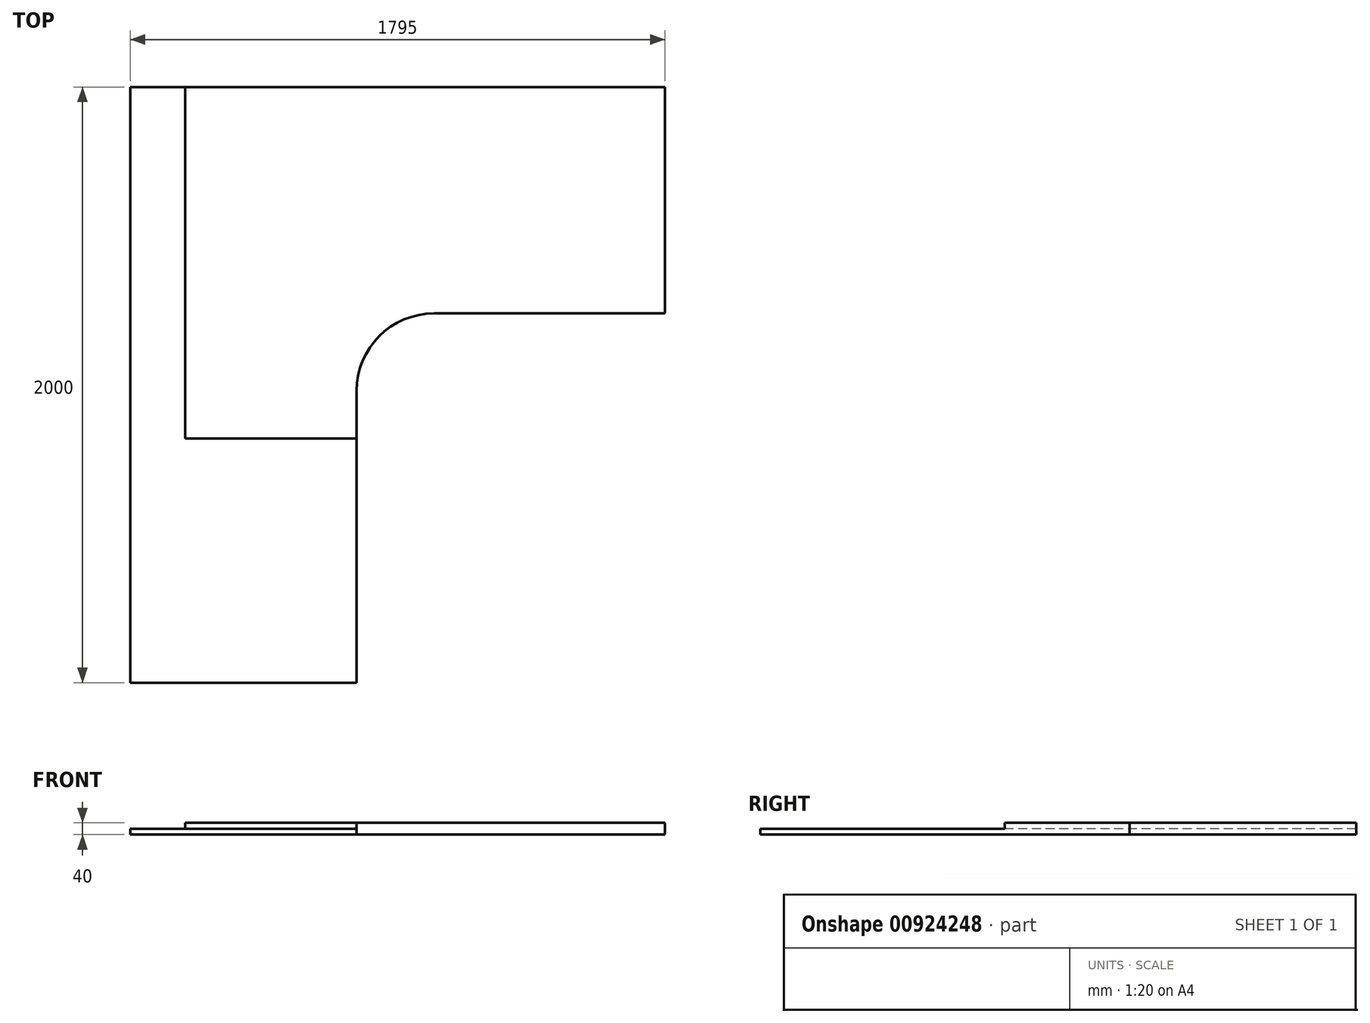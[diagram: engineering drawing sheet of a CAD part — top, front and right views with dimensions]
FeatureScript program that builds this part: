
annotation { "Feature Type Name" : "Feature", "Feature Type Description" : "" }
export const myFeature = defineFeature(function(context is Context, id is Id, definition is map)
    precondition{}
    {
        {
            assignVariable(context, id + "F0", {"name" : "hL", "anyValue" : 970});
        }
        {
            assignVariable(context, id + "F1", {"name" : "hd", "anyValue" : 740});
        }
        {
            var Q0;
            Q0=qCreatedBy(makeId("Top.planeOp"),FACE);
            var sketch = newSketch(context, id + "F2", { "sketchPlane" : qUnion([Q0])});
            skLineSegment(sketch, "E0.bottom", {"start": v(-760, 760) * mm, "end": v(1035, 760) * mm});
            skLineSegment(sketch, "E0.top", {"start": v(-760, -1240) * mm, "end": v(1035, -1240) * mm});
            skLineSegment(sketch, "E0.left", {"start": v(-760, 760) * mm, "end": v(-760, -1240) * mm});
            skLineSegment(sketch, "E0.right", {"start": v(1035, 760) * mm, "end": v(1035, -1240) * mm});
            skSolve(sketch);
        }
        {
            var Q0;
            Q0=qCreatedBy(makeId("Top.planeOp"),FACE);
            cPlane(context, id + "F3", {"entities" : qUnion([Q0]), "cplaneType" : CPlaneType.OFFSET, "offset" : (getVariable(context, 'hd') - 20) * mm, "width" : 150 * mm, "height" : 150 * mm});
        }
        {
            var Q0;
            Q0=qCreatedBy(id+"F3.planeOp",FACE);
            var sketch = newSketch(context, id + "F4", { "sketchPlane" : qUnion([Q0])});
            skPoint(sketch, "E1.0", {"position": v(1035, 760) * mm});
            skPoint(sketch, "E2.0", {"position": v(-760, 760) * mm});
            skPoint(sketch, "E3.0", {"position": v(-760, -1240) * mm});
            skLineSegment(sketch, "E4", {"start": v(260, 0) * mm, "end": v(1035, 0) * mm});
            skLineSegment(sketch, "E5", {"start": v(1035, 0) * mm, "end": v(1035, 760) * mm});
            skLineSegment(sketch, "E6", {"start": v(-760, 760) * mm, "end": v(-760, -1240) * mm});
            skLineSegment(sketch, "E7", {"start": v(0, -1240) * mm, "end": v(0, -260) * mm});
            skLineSegment(sketch, "E8", {"start": v(-760, 760) * mm, "end": v(1035, 760) * mm});
            skLineSegment(sketch, "E9", {"start": v(-760, -1240) * mm, "end": v(0, -1240) * mm});
            skPoint(sketch, "E10.visualSharp", {"position": v(0, 0) * mm});
            skArc(sketch, "E10.filletArc", {"start": v(260, 0) * mm, "mid": v(76.15, -76.15) * mm, "end": v(0, -260) * mm});
            skLineSegment(sketch, "E11", {"start": v(-575, 760) * mm, "end": v(-575, -420) * mm});
            skLineSegment(sketch, "E12", {"start": v(-575, -420) * mm, "end": v(0, -420) * mm});
            skSolve(sketch);
        }
        {
            var Q0;
            Q0=makeQuery(id+"F4.imprint","IMPRINT",FACE,{"disambiguationData":[TD([[makeQuery(id+"F4.imprint","IMPRINT",EDGE,{"derivedFrom":sQuery(id+"F4.wireOp",EDGE,"E4")}),1.0]])]});
            extrude(context, id + "F5", {"entities" : qUnion([Q0]), "depth" : 20 * mm, "offsetDistance" : 25 * mm});
        }
        {
            var Q0;
            Q0 = qSketchRegion(id + "F4", true);
            extrude(context, id + "F6", {"entities" : qUnion([Q0]), "operationType" : NewBodyOperationType.ADD, "oppositeDirection" : true, "depth" : 20 * mm, "offsetDistance" : 25 * mm});
        }
        {
            var Q0;
            Q0=qCreatedBy(makeId("Top.planeOp"),FACE);
            cPlane(context, id + "F7", {"entities" : qUnion([Q0]), "cplaneType" : CPlaneType.OFFSET, "offset" : (getVariable(context, 'hd') + getVariable(context, 'hL')) * mm, "width" : 150 * mm, "height" : 150 * mm});
        }
        {
            var Q0;
            Q0=qCreatedBy(id+"F7.planeOp",FACE);
            var sketch = newSketch(context, id + "F8", { "sketchPlane" : qUnion([Q0])});
            skPoint(sketch, "E13", {"position": v(-340, -315) * mm});
            skPoint(sketch, "E14", {"position": v(640, 330) * mm});
            skPoint(sketch, "E15.0", {"position": v(260, -260) * mm});
            skArc(sketch, "E16.0", {"start": v(260, 340) * mm, "mid": v(-164.26, 164.26) * mm, "end": v(-340, -260) * mm, "construction": true});
            skPoint(sketch, "E17.0", {"position": v(-760, 760) * mm});
            skLineSegment(sketch, "E18", {"start": v(-760, 760) * mm, "end": v(260, -260) * mm, "construction": true});
            skPoint(sketch, "E19", {"position": v(-75, 235) * mm});
            skPoint(sketch, "E20", {"position": v(700, 330) * mm});
            skSolve(sketch);
        }
        {
            var Q0;
            Q0=qCreatedBy(makeId("Top.planeOp"),FACE);
            var sketch = newSketch(context, id + "F9", { "sketchPlane" : qUnion([Q0])});
            skPoint(sketch, "E21.0", {"position": v(-75, 235) * mm});
            skCircle(sketch, "E22", {"center": v(-75, 235) * mm, "radius": 555.61 * mm});
            skPoint(sketch, "E23.0", {"position": v(640, 330) * mm});
            skPoint(sketch, "E24.0", {"position": v(-340, -315) * mm});
            skCircle(sketch, "E25", {"center": v(640, 330) * mm, "radius": 555.61 * mm});
            skCircle(sketch, "E26", {"center": v(-340, -315) * mm, "radius": 555.61 * mm});
            skPoint(sketch, "E27.0", {"position": v(700, 330) * mm});
            skCircle(sketch, "E28", {"center": v(700, 330) * mm, "radius": 555.61 * mm});
            skSolve(sketch);
        }
        {
            var Q0;
            Q0=makeQuery(id+"F9.imprint","IMPRINT",FACE,{"disambiguationData":[TD([[makeQuery(id+"F9.imprint","IMPRINT",EDGE,{"derivedFrom":sQuery(id+"F9.wireOp",EDGE,"E22")}),1.0]])]});
            var Q1;
            Q1=sQuery(id+"F8.wireOp",VERTEX,"cbbe6bf4-1df4-4786-b697-ca3d39312b80");
            var Q2;
            Q2=sQuery(id+"F9.wireOp",EDGE,"E22");
            var Q3;
            Q3=sQuery(id+"F8.wireOp",VERTEX,"E19");
            loft(context, id + "F10", {"bodyType" : ToolBodyType.SURFACE, "sheetProfilesArray" : [{ "sheetProfileEntities" : qUnion([Q0]) }, { "sheetProfileEntities" : qUnion([Q1]) }], "wireProfilesArray" : [{ "wireProfileEntities" : qUnion([Q2]) }, { "wireProfileEntities" : qUnion([Q3]) }]});
        }
        {
            var Q1;
            {var subQ0=sQuery(id+"F9.wireOp",EDGE,"E25");var subQ1=sQuery(id+"F9.wireOp",EDGE,"E22");var subQ2=makeQuery(id+"F9.imprint","INTERSECT",VERTEX,{"disambiguationData":[OD(0.0)],"derivedFrom":[subQ1,subQ0]});Q1=makeQuery(id+"F9.imprint","IMPRINT",FACE,{"disambiguationData":[TD([[makeQuery(id+"F9.imprint","IMPRINT",EDGE,{"disambiguationData":[TD([[subQ2,1.0]])],"derivedFrom":subQ1}),-1.0]])]});}
            var Q2;
            {var subQ0=sQuery(id+"F9.wireOp",EDGE,"E25");var subQ1=sQuery(id+"F9.wireOp",EDGE,"E22");var subQ2=makeQuery(id+"F9.imprint","INTERSECT",VERTEX,{"disambiguationData":[OD(1.0)],"derivedFrom":[subQ1,subQ0]});Q2=makeQuery(id+"F9.imprint","IMPRINT",FACE,{"disambiguationData":[TD([[makeQuery(id+"F9.imprint","IMPRINT",EDGE,{"disambiguationData":[TD([[subQ2,-1.0]])],"derivedFrom":subQ1}),1.0]])]});}
            var Q3;
            {var subQ0=sQuery(id+"F9.wireOp",EDGE,"E25");var subQ1=sQuery(id+"F9.wireOp",EDGE,"E22");var subQ2=makeQuery(id+"F9.imprint","INTERSECT",VERTEX,{"disambiguationData":[OD(0.0)],"derivedFrom":[subQ1,subQ0]});Q3=makeQuery(id+"F9.imprint","IMPRINT",FACE,{"disambiguationData":[TD([[makeQuery(id+"F9.imprint","IMPRINT",EDGE,{"disambiguationData":[TD([[subQ2,1.0]])],"derivedFrom":subQ1}),1.0]])]});}
            var Q4;
            Q4=sQuery(id+"F8.wireOp",VERTEX,"E14");
            var Q5;
            Q5=sQuery(id+"F9.wireOp",EDGE,"E25");
            var Q6;
            Q6=sQuery(id+"F8.wireOp",VERTEX,"E14");
            loft(context, id + "F11", {"bodyType" : ToolBodyType.SURFACE, "sheetProfilesArray" : [{ "sheetProfileEntities" : qUnion([Q1]) }, { "sheetProfileEntities" : qUnion([Q2]) }, { "sheetProfileEntities" : qUnion([Q3]) }, { "sheetProfileEntities" : qUnion([Q4]) }], "wireProfilesArray" : [{ "wireProfileEntities" : qUnion([Q5]) }, { "wireProfileEntities" : qUnion([Q6]) }]});
        }
        {
            var Q0;
            Q0=sQuery(id+"F9.wireOp",EDGE,"E26");
            var Q1;
            Q1=sQuery(id+"F8.wireOp",VERTEX,"E13");
            loft(context, id + "F12", {"bodyType" : ToolBodyType.SURFACE, "wireProfilesArray" : [{ "wireProfileEntities" : qUnion([Q0]) }, { "wireProfileEntities" : qUnion([Q1]) }]});
        }
    });
